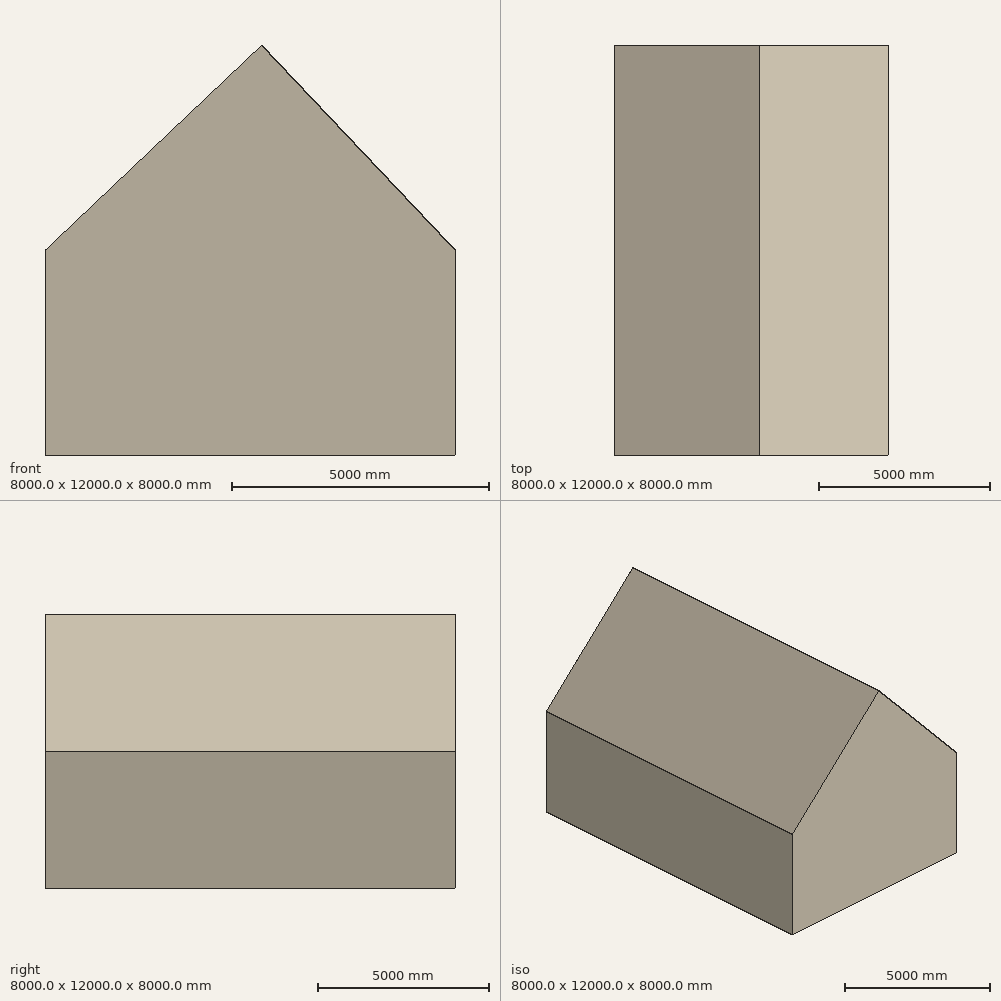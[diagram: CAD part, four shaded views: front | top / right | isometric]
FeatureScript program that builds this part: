
annotation { "Feature Type Name" : "Feature", "Feature Type Description" : "" }
export const myFeature = defineFeature(function(context is Context, id is Id, definition is map)
    precondition{}
    {
        {
            var Q0;
            Q0=qCreatedBy(makeId("Front.planeOp"),FACE);
            var sketch = newSketch(context, id + "F0", { "sketchPlane" : qUnion([Q0])});
            skLineSegment(sketch, "E0.bottom", {"start": v(0, 0) * mm, "end": v(8000, 0) * mm});
            skLineSegment(sketch, "E0.top", {"start": v(0, -4000) * mm, "end": v(8000, -4000) * mm});
            skLineSegment(sketch, "E0.left", {"start": v(0, 0) * mm, "end": v(0, -4000) * mm});
            skLineSegment(sketch, "E0.right", {"start": v(8000, 0) * mm, "end": v(8000, -4000) * mm});
            skLineSegment(sketch, "E1", {"start": v(0, 0) * mm, "end": v(4222.6, 4000) * mm});
            skLineSegment(sketch, "E2", {"start": v(4222.6, 4000) * mm, "end": v(8000, 0) * mm});
            skSolve(sketch);
        }
        {
            var Q0;
            Q0=makeQuery(id+"F0.imprint","IMPRINT",FACE,{"disambiguationData":[TD([[makeQuery(id+"F0.imprint","IMPRINT",EDGE,{"derivedFrom":sQuery(id+"F0.wireOp",EDGE,"E0.bottom")}),-1.0]])]});
            extrude(context, id + "F1", {"entities" : qUnion([Q0]), "depth" : 12000 * mm});
        }
        {
            var Q0;
            Q0 = qSketchRegion(id + "F0", true);
            extrude(context, id + "F2", {"entities" : qUnion([Q0]), "operationType" : NewBodyOperationType.ADD, "depth" : 12000 * mm});
        }
    });
